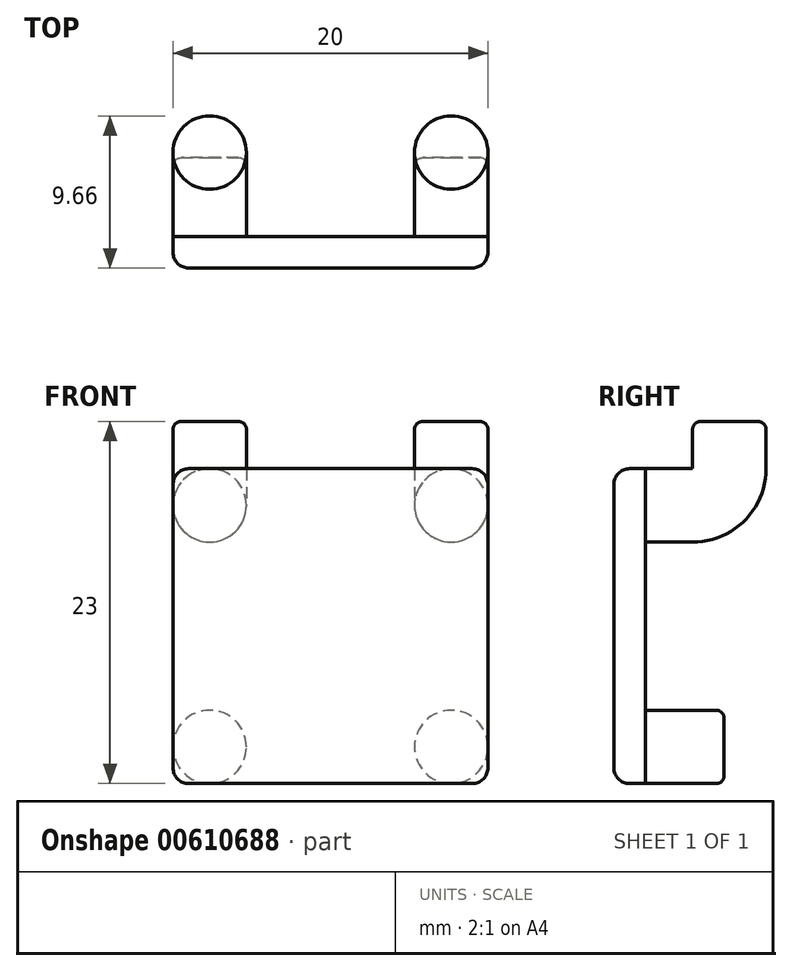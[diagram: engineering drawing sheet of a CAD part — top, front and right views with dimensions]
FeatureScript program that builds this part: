
annotation { "Feature Type Name" : "Feature", "Feature Type Description" : "" }
export const myFeature = defineFeature(function(context is Context, id is Id, definition is map)
    precondition{}
    {
        {
            var Q0;
            Q0=qCreatedBy(makeId("Front.planeOp"),FACE);
            var sketch = newSketch(context, id + "F0", { "sketchPlane" : qUnion([Q0])});
            skCircle(sketch, "E0", {"center": v(-7.93, 15.34) * mm, "radius": 2.33 * mm});
            skCircle(sketch, "E1", {"center": v(7.41, 15.34) * mm, "radius": 2.33 * mm});
            skCircle(sketch, "E2", {"center": v(7.41, 0) * mm, "radius": 2.33 * mm});
            skCircle(sketch, "E3", {"center": v(-7.93, 0) * mm, "radius": 2.33 * mm});
            skLineSegment(sketch, "E4", {"start": v(-7.93, 2.33) * mm, "end": v(-7.93, 13.01) * mm});
            skLineSegment(sketch, "E5", {"start": v(-5.6, 15.34) * mm, "end": v(5.08, 15.34) * mm});
            skLineSegment(sketch, "E6", {"start": v(7.41, 2.33) * mm, "end": v(7.41, 13.01) * mm});
            skLineSegment(sketch, "E7", {"start": v(5.08, 0) * mm, "end": v(-5.6, 0) * mm});
            skLineSegment(sketch, "E8.bottom", {"start": v(-10.26, 17.67) * mm, "end": v(9.74, 17.67) * mm});
            skLineSegment(sketch, "E8.top", {"start": v(-10.26, -2.33) * mm, "end": v(9.74, -2.33) * mm});
            skLineSegment(sketch, "E8.left", {"start": v(-10.26, 17.67) * mm, "end": v(-10.26, -2.33) * mm});
            skLineSegment(sketch, "E8.right", {"start": v(9.74, 17.67) * mm, "end": v(9.74, -2.33) * mm});
            skSolve(sketch);
        }
        {
            var Q0;
            {var subQ0=sQuery(id+"F0.wireOp",EDGE,"E0");var subQ1=makeQuery(id+"F0.imprint","INTERSECT",VERTEX,{"derivedFrom":[subQ0,sQuery(id+"F0.wireOp",EDGE,"E5")]});Q0=makeQuery(id+"F0.imprint","IMPRINT",FACE,{"disambiguationData":[TD([[makeQuery(id+"F0.imprint","IMPRINT",EDGE,{"disambiguationData":[TD([[subQ1,-1.0]])],"derivedFrom":subQ0}),1.0]])]});}
            var Q1;
            {var subQ0=sQuery(id+"F0.wireOp",EDGE,"E1");var subQ1=makeQuery(id+"F0.imprint","INTERSECT",VERTEX,{"derivedFrom":[subQ0,sQuery(id+"F0.wireOp",EDGE,"E8.bottom")]});Q1=makeQuery(id+"F0.imprint","IMPRINT",FACE,{"disambiguationData":[TD([[makeQuery(id+"F0.imprint","IMPRINT",EDGE,{"disambiguationData":[TD([[subQ1,1.0]])],"derivedFrom":subQ0}),1.0]])]});}
            extrude(context, id + "F1", {"entities" : qUnion([Q0, Q1]), "oppositeDirection" : true, "depth" : 3 * mm, "offsetDistance" : 25 * mm});
        }
        {
            var Q0;
            {var subQ0=sQuery(id+"F0.wireOp",EDGE,"E3");var subQ1=makeQuery(id+"F0.imprint","INTERSECT",VERTEX,{"derivedFrom":[subQ0,sQuery(id+"F0.wireOp",EDGE,"E4")]});Q0=makeQuery(id+"F0.imprint","IMPRINT",FACE,{"disambiguationData":[TD([[makeQuery(id+"F0.imprint","IMPRINT",EDGE,{"disambiguationData":[TD([[subQ1,1.0]])],"derivedFrom":subQ0}),1.0]])]});}
            var Q1;
            {var subQ0=sQuery(id+"F0.wireOp",EDGE,"E2");var subQ1=makeQuery(id+"F0.imprint","INTERSECT",VERTEX,{"derivedFrom":[subQ0,sQuery(id+"F0.wireOp",EDGE,"E6")]});Q1=makeQuery(id+"F0.imprint","IMPRINT",FACE,{"disambiguationData":[TD([[makeQuery(id+"F0.imprint","IMPRINT",EDGE,{"disambiguationData":[TD([[subQ1,1.0]])],"derivedFrom":subQ0}),1.0]])]});}
            extrude(context, id + "F2", {"entities" : qUnion([Q0, Q1]), "oppositeDirection" : true, "depth" : 5 * mm, "offsetDistance" : 25 * mm});
        }
        {
            var Q0;
            Q0=makeQuery(id+"F1.opExtrude","CAP_FACE",FACE,{"disambiguationData":[OSD([sQuery(id+"F0.wireOp",EDGE,"E1")])],"isStart":false});
            var sketch = newSketch(context, id + "F3", { "sketchPlane" : qUnion([Q0])});
            skLineSegment(sketch, "E9", {"start": v(-7.41, 15.34) * mm, "end": v(7.93, 15.34) * mm});
            skLineSegment(sketch, "E10", {"start": v(-7.41, 17.67) * mm, "end": v(7.93, 17.67) * mm});
            skSolve(sketch);
        }
        {
            var Q0;
            Q0=makeQuery(id+"F1.opExtrude","CAP_FACE",FACE,{"disambiguationData":[OSD([sQuery(id+"F0.wireOp",EDGE,"E0")])],"isStart":false});
            var Q1;
            Q1=makeQuery(id+"F3.imprint","IMPRINT",FACE,{"disambiguationData":[TD([[makeQuery(id+"F3.imprint","IMPRINT",EDGE,{"derivedFrom":makeQuery(id+"F1.opExtrude","CAP_EDGE",EDGE,{"disambiguationData":[OSD([sQuery(id+"F0.wireOp",EDGE,"E1")])],"isStart":false})}),-1.0]])]});
            var Q2;
            Q2=sQuery(id+"F3.wireOp",EDGE,"E10");
            revolve(context, id + "F4", {"operationType" : NewBodyOperationType.ADD, "entities" : qUnion([Q0, Q1]), "axis" : qUnion([Q2]), "revolveType" : RevolveType.ONE_DIRECTION, "oppositeDirection" : true, "angle" : 90 * degree});
        }
        {
            var Q0;
            Q0=makeQuery(id+"F4.opRevolve","CAP_FACE",FACE,{"disambiguationData":[OSD([sQuery(id+"F0.wireOp",EDGE,"E1")])],"isStart":false});
            var Q1;
            Q1=makeQuery(id+"F4.opRevolve","CAP_FACE",FACE,{"disambiguationData":[OSD([sQuery(id+"F0.wireOp",EDGE,"E0")])],"isStart":false});
            extrude(context, id + "F5", {"entities" : qUnion([Q0, Q1]), "operationType" : NewBodyOperationType.ADD, "depth" : 3 * mm, "offsetDistance" : 25 * mm});
        }
        {
            var Q0;
            {var subQ0=sQuery(id+"F0.wireOp",EDGE,"E8.left");var subQ1=sQuery(id+"F0.wireOp",EDGE,"E3");var subQ2=makeQuery(id+"F0.imprint","INTERSECT",VERTEX,{"derivedFrom":[subQ1,subQ0]});Q0=makeQuery(id+"F0.imprint","IMPRINT",FACE,{"disambiguationData":[TD([[makeQuery(id+"F0.imprint","IMPRINT",EDGE,{"disambiguationData":[TD([[subQ2,-1.0]])],"derivedFrom":subQ1}),-1.0]])]});}
            var Q1;
            {var subQ0=sQuery(id+"F0.wireOp",EDGE,"E3");var subQ1=makeQuery(id+"F0.imprint","INTERSECT",VERTEX,{"derivedFrom":[subQ0,sQuery(id+"F0.wireOp",EDGE,"E4")]});Q1=makeQuery(id+"F0.imprint","IMPRINT",FACE,{"disambiguationData":[TD([[makeQuery(id+"F0.imprint","IMPRINT",EDGE,{"disambiguationData":[TD([[subQ1,1.0]])],"derivedFrom":subQ0}),1.0]])]});}
            var Q2;
            {var subQ0=sQuery(id+"F0.wireOp",EDGE,"E5");Q2=makeQuery(id+"F0.imprint","IMPRINT",FACE,{"disambiguationData":[TD([[makeQuery(id+"F0.imprint","IMPRINT",EDGE,{"derivedFrom":subQ0}),1.0]])]});}
            var Q3;
            {var subQ0=sQuery(id+"F0.wireOp",EDGE,"E4");Q3=makeQuery(id+"F0.imprint","IMPRINT",FACE,{"disambiguationData":[TD([[makeQuery(id+"F0.imprint","IMPRINT",EDGE,{"derivedFrom":subQ0}),1.0]])]});}
            var Q4;
            {var subQ0=sQuery(id+"F0.wireOp",EDGE,"E8.bottom");var subQ1=sQuery(id+"F0.wireOp",EDGE,"E0");var subQ2=makeQuery(id+"F0.imprint","INTERSECT",VERTEX,{"derivedFrom":[subQ1,subQ0]});Q4=makeQuery(id+"F0.imprint","IMPRINT",FACE,{"disambiguationData":[TD([[makeQuery(id+"F0.imprint","IMPRINT",EDGE,{"disambiguationData":[TD([[subQ2,-1.0]])],"derivedFrom":subQ1}),-1.0]])]});}
            var Q5;
            {var subQ0=sQuery(id+"F0.wireOp",EDGE,"E4");Q5=makeQuery(id+"F0.imprint","IMPRINT",FACE,{"disambiguationData":[TD([[makeQuery(id+"F0.imprint","IMPRINT",EDGE,{"derivedFrom":subQ0}),-1.0]])]});}
            var Q6;
            {var subQ0=sQuery(id+"F0.wireOp",EDGE,"E0");var subQ1=makeQuery(id+"F0.imprint","INTERSECT",VERTEX,{"derivedFrom":[subQ0,sQuery(id+"F0.wireOp",EDGE,"E5")]});Q6=makeQuery(id+"F0.imprint","IMPRINT",FACE,{"disambiguationData":[TD([[makeQuery(id+"F0.imprint","IMPRINT",EDGE,{"disambiguationData":[TD([[subQ1,-1.0]])],"derivedFrom":subQ0}),1.0]])]});}
            var Q7;
            {var subQ0=sQuery(id+"F0.wireOp",EDGE,"E7");Q7=makeQuery(id+"F0.imprint","IMPRINT",FACE,{"disambiguationData":[TD([[makeQuery(id+"F0.imprint","IMPRINT",EDGE,{"derivedFrom":subQ0}),1.0]])]});}
            var Q8;
            {var subQ0=sQuery(id+"F0.wireOp",EDGE,"E6");Q8=makeQuery(id+"F0.imprint","IMPRINT",FACE,{"disambiguationData":[TD([[makeQuery(id+"F0.imprint","IMPRINT",EDGE,{"derivedFrom":subQ0}),-1.0]])]});}
            var Q9;
            {var subQ0=sQuery(id+"F0.wireOp",EDGE,"E1");var subQ1=makeQuery(id+"F0.imprint","INTERSECT",VERTEX,{"derivedFrom":[subQ0,sQuery(id+"F0.wireOp",EDGE,"E8.bottom")]});Q9=makeQuery(id+"F0.imprint","IMPRINT",FACE,{"disambiguationData":[TD([[makeQuery(id+"F0.imprint","IMPRINT",EDGE,{"disambiguationData":[TD([[subQ1,1.0]])],"derivedFrom":subQ0}),1.0]])]});}
            var Q10;
            {var subQ0=sQuery(id+"F0.wireOp",EDGE,"E2");var subQ1=makeQuery(id+"F0.imprint","INTERSECT",VERTEX,{"derivedFrom":[subQ0,sQuery(id+"F0.wireOp",EDGE,"E6")]});Q10=makeQuery(id+"F0.imprint","IMPRINT",FACE,{"disambiguationData":[TD([[makeQuery(id+"F0.imprint","IMPRINT",EDGE,{"disambiguationData":[TD([[subQ1,1.0]])],"derivedFrom":subQ0}),1.0]])]});}
            var Q11;
            {var subQ0=sQuery(id+"F0.wireOp",EDGE,"E8.right");var subQ1=sQuery(id+"F0.wireOp",EDGE,"E2");var subQ2=makeQuery(id+"F0.imprint","INTERSECT",VERTEX,{"derivedFrom":[subQ1,subQ0]});Q11=makeQuery(id+"F0.imprint","IMPRINT",FACE,{"disambiguationData":[TD([[makeQuery(id+"F0.imprint","IMPRINT",EDGE,{"disambiguationData":[TD([[subQ2,1.0]])],"derivedFrom":subQ1}),-1.0]])]});}
            var Q12;
            {var subQ0=sQuery(id+"F0.wireOp",EDGE,"E8.bottom");var subQ1=sQuery(id+"F0.wireOp",EDGE,"E1");var subQ2=makeQuery(id+"F0.imprint","INTERSECT",VERTEX,{"derivedFrom":[subQ1,subQ0]});Q12=makeQuery(id+"F0.imprint","IMPRINT",FACE,{"disambiguationData":[TD([[makeQuery(id+"F0.imprint","IMPRINT",EDGE,{"disambiguationData":[TD([[subQ2,1.0]])],"derivedFrom":subQ1}),-1.0]])]});}
            extrude(context, id + "F6", {"entities" : qUnion([Q0, Q1, Q2, Q3, Q4, Q5, Q6, Q7, Q8, Q9, Q10, Q11, Q12]), "depth" : 2 * mm, "offsetDistance" : 25 * mm});
        }
        {
            var Q0;
            Q0=makeQuery(id+"F6.opExtrude","CAP_EDGE",EDGE,{"disambiguationData":[OSD([sQuery(id+"F0.wireOp",EDGE,"E8.bottom")])],"isStart":false});
            var Q1;
            Q1=makeQuery(id+"F6.opExtrude","CAP_EDGE",EDGE,{"disambiguationData":[OSD([sQuery(id+"F0.wireOp",EDGE,"E8.left")])],"isStart":false});
            var Q2;
            Q2=makeQuery(id+"F6.opExtrude","CAP_EDGE",EDGE,{"disambiguationData":[OSD([sQuery(id+"F0.wireOp",EDGE,"E8.top")])],"isStart":false});
            var Q3;
            Q3=makeQuery(id+"F6.opExtrude","CAP_EDGE",EDGE,{"disambiguationData":[OSD([sQuery(id+"F0.wireOp",EDGE,"E8.right")])],"isStart":false});
            var Q4;
            Q4=makeQuery(id+"F6.opExtrude","SWEPT_EDGE",EDGE,{"disambiguationData":[OSD([sQuery(id+"F0.wireOp",EDGE,"E8.top"),sQuery(id+"F0.wireOp",EDGE,"E8.left")])]});
            var Q5;
            Q5=makeQuery(id+"F6.opExtrude","SWEPT_EDGE",EDGE,{"disambiguationData":[OSD([sQuery(id+"F0.wireOp",EDGE,"E8.bottom"),sQuery(id+"F0.wireOp",EDGE,"E8.left")])]});
            var Q6;
            Q6=makeQuery(id+"F6.opExtrude","SWEPT_EDGE",EDGE,{"disambiguationData":[OSD([sQuery(id+"F0.wireOp",EDGE,"E8.bottom"),sQuery(id+"F0.wireOp",EDGE,"E8.right")])]});
            var Q7;
            Q7=makeQuery(id+"F6.opExtrude","SWEPT_EDGE",EDGE,{"disambiguationData":[OSD([sQuery(id+"F0.wireOp",EDGE,"E8.top"),sQuery(id+"F0.wireOp",EDGE,"E8.right")])]});
            fillet(context, id + "F7", {"entities" : qUnion([Q0, Q1, Q2, Q3, Q4, Q5, Q6, Q7]), "radius" : 1 * mm, "tangentPropagation" : true, "allowEdgeOverflow" : false});
        }
        {
            var Q0;
            Q0=makeQuery(id+"F5.opExtrude","CAP_FACE",FACE,{"disambiguationData":[OSD([sQuery(id+"F0.wireOp",EDGE,"E0")])],"isStart":false});
            var Q1;
            Q1=makeQuery(id+"F5.opExtrude","CAP_FACE",FACE,{"disambiguationData":[OSD([sQuery(id+"F0.wireOp",EDGE,"E1")])],"isStart":false});
            var Q2;
            Q2=makeQuery(id+"F2.opExtrude","CAP_EDGE",EDGE,{"disambiguationData":[OSD([sQuery(id+"F0.wireOp",EDGE,"E2")])],"isStart":false});
            var Q3;
            Q3=makeQuery(id+"F2.opExtrude","CAP_EDGE",EDGE,{"disambiguationData":[OSD([sQuery(id+"F0.wireOp",EDGE,"E3")])],"isStart":false});
            fillet(context, id + "F8", {"entities" : qUnion([Q0, Q1, Q2, Q3]), "radius" : 0.5 * mm, "tangentPropagation" : true, "allowEdgeOverflow" : false});
        }
    });
